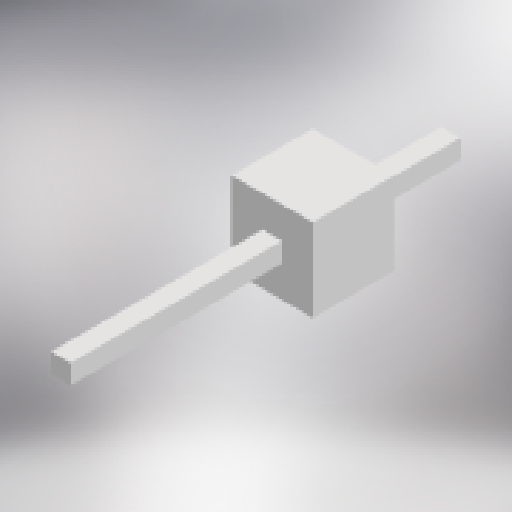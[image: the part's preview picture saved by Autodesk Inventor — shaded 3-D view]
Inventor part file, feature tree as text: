
AUTODESK INVENTOR PART (.ipt)
format: ipt  version: 2024 (Build 280153000, 153)  size: 164,352 bytes
history: native  units: mm
features: extrude x2, sketch x2, plane x1, projected_geometry x1
ambient origin geometry x8: Origin, YZ Plane, XZ Plane, XY Plane, X Axis, Y Axis, Z Axis, Center Point
bodies: Solid1 (feature_tree)
feature tree (6):
  extrude  "Extrusion1"  Depth=0.6mm
  sketch  "Sketch3"  dims[d4=10.0mm d5=2.0mm d6=0.0mm d7=0.0mm d8=2.54mm d9=2.5mm d10=-3.0mm d11=2.5mm d12=0.0mm]
  plane  "Work Plane1"
  extrude  "Extrusion2"  Depth=2.54mm
  sketch  "Sketch2"  dims[d2=0.6mm d3=0.6mm]
  projected_geometry  "Projected Loop1"
